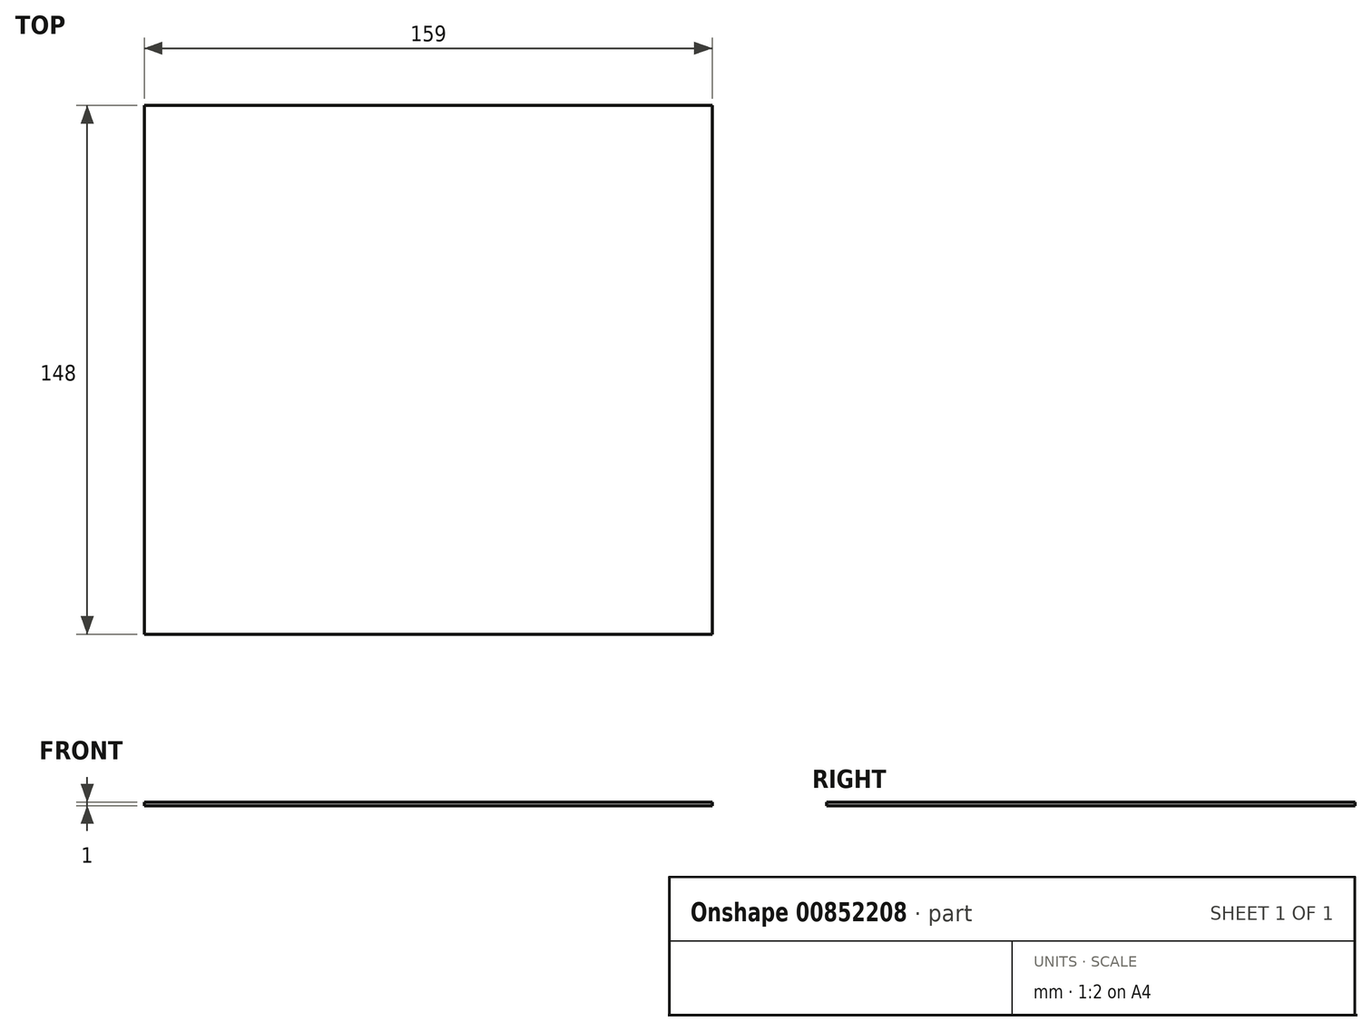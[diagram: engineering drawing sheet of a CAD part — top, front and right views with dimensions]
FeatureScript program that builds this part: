
annotation { "Feature Type Name" : "Feature", "Feature Type Description" : "" }
export const myFeature = defineFeature(function(context is Context, id is Id, definition is map)
    precondition{}
    {
        {
            var Q0;
            Q0=qCreatedBy(makeId("Top.planeOp"),FACE);
            var sketch = newSketch(context, id + "F0", { "sketchPlane" : qUnion([Q0])});
            skLineSegment(sketch, "E0.bottom", {"start": v(-75.75, 81.95) * mm, "end": v(83.25, 81.95) * mm});
            skLineSegment(sketch, "E0.top", {"start": v(-75.75, -66.05) * mm, "end": v(83.25, -66.05) * mm});
            skLineSegment(sketch, "E0.left", {"start": v(-75.75, 81.95) * mm, "end": v(-75.75, -66.05) * mm});
            skLineSegment(sketch, "E0.right", {"start": v(83.25, 81.95) * mm, "end": v(83.25, -66.05) * mm});
            skSolve(sketch);
        }
        {
            var Q0;
            Q0=makeQuery(id+"F0.imprint","IMPRINT",FACE,{"disambiguationData":[TD([[makeQuery(id+"F0.imprint","IMPRINT",EDGE,{"derivedFrom":sQuery(id+"F0.wireOp",EDGE,"E0.bottom")}),-1.0]])]});
            extrude(context, id + "F1", {"entities" : qUnion([Q0]), "depth" : 1 * mm, "offsetDistance" : 25.4 * mm});
        }
    });
